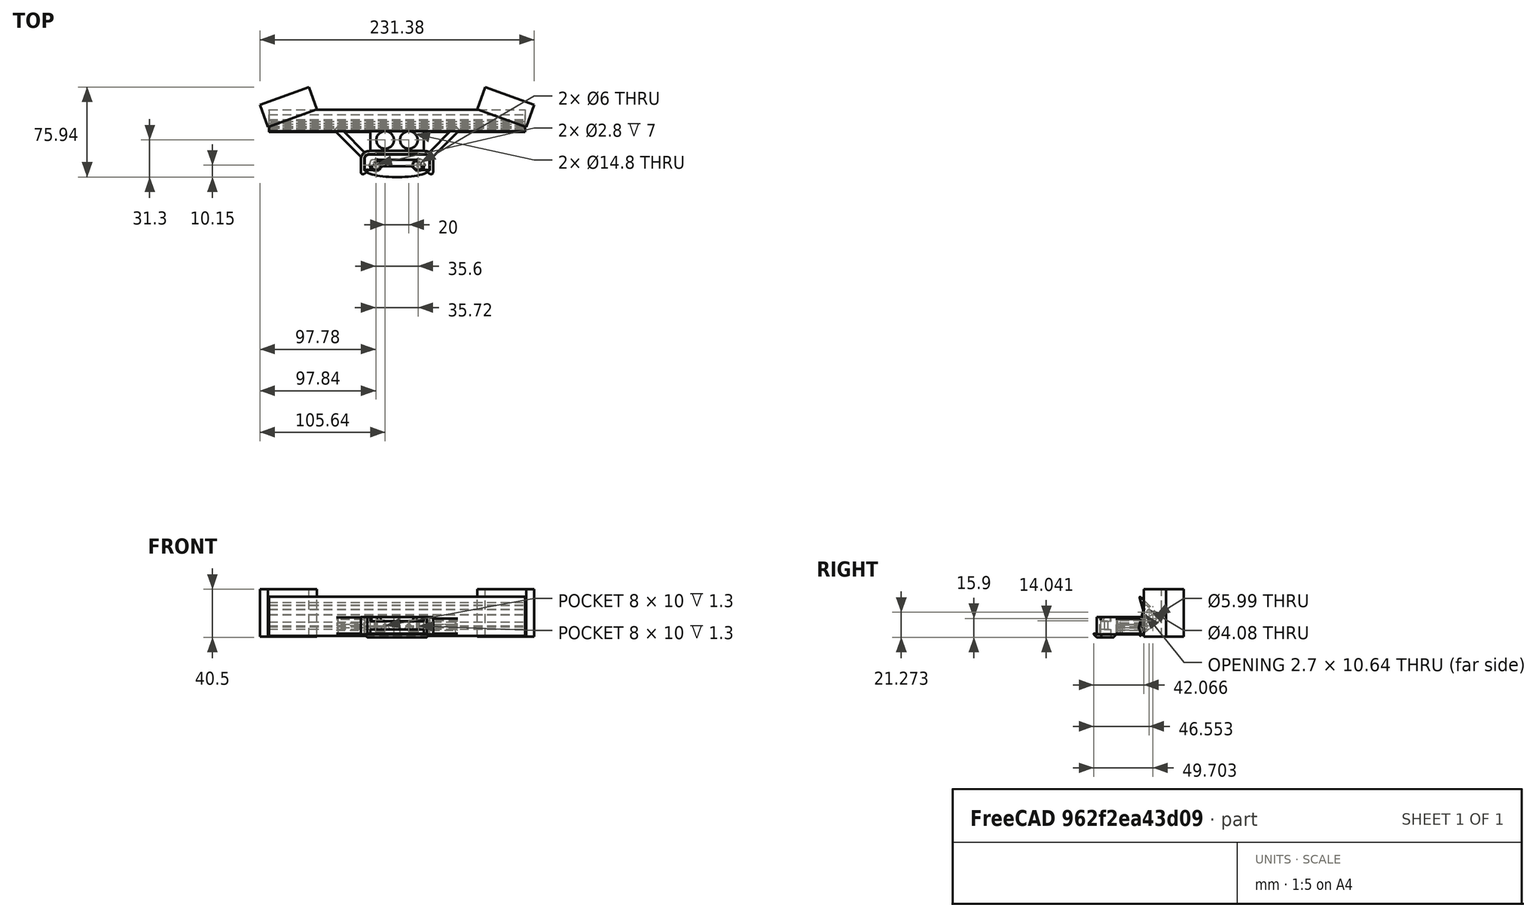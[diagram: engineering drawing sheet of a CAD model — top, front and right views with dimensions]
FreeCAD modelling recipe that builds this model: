
FCSTD DOCUMENT  (FreeCAD 0.21R0.20.1)
Label: 056
License: All rights reserved
LicenseURL: http://en.wikipedia.org/wiki/All_rights_reserved
objects: Part::Cylinder×20, Part::MultiFuse×13, Sketcher::SketchObject×7, Part::Extrusion×7, Part::Box×7, Part::Fillet×5, Part::Cut×4, Part::Chamfer×2
note: 65 computed .brp shape members not serialized (recipe doc carries the construction recipe); baked Part::Feature solids carry a one-line shape summary decoded from their .brp

FEATURE [Sketcher::SketchObject] Sketch  label="attatchmentPiece"
  FullyConstrained = true
  sketch-geometry (20):
    g0: LineSegment StartX=21.05 StartY=0 StartZ=0 EndX=21.05 EndY=-1 EndZ=0
    g1: LineSegment StartX=21.05 StartY=-1 StartZ=0 EndX=21.05 EndY=-4.3 EndZ=0
    g2: LineSegment StartX=-24.15 StartY=4.3 StartZ=0 EndX=21.05 EndY=4.3 EndZ=0
    g3: LineSegment StartX=21.05 StartY=0 StartZ=0 EndX=21.05 EndY=4.3 EndZ=0
    g4-g7: Circle x4 (B-spline internal-alignment scaffolding for g8; pole/knot coordinates omitted)
    g8: BSplineCurve PolesCount=4 KnotsCount=2 Degree=3 IsPeriodic=0
    g9: GeomPoint X=10.05 Y=-1 Z=0
    g10: GeomPoint X=14.55 Y=-4.3 Z=0
    g11: LineSegment StartX=10.05 StartY=-1 StartZ=0 EndX=-10.05 EndY=-1 EndZ=0
    g12: LineSegment StartX=14.55 StartY=-4.3 StartZ=0 EndX=21.05 EndY=-4.3 EndZ=0
    g13: LineSegment StartX=-24.15 StartY=4.3 StartZ=0 EndX=-24.15 EndY=-4.3 EndZ=0
    g14: LineSegment StartX=-13.15 StartY=-1 StartZ=0 EndX=-10.05 EndY=-1 EndZ=0
    g15: LineSegment StartX=-24.15 StartY=-4.3 StartZ=0 EndX=-19.35 EndY=-4.3 EndZ=0
    g16: LineSegment StartX=-19.35 StartY=-4.3 StartZ=0 EndX=-17.65 EndY=-4.3 EndZ=0
    g17: BSplineCurve PolesCount=4 KnotsCount=2 Degree=3 IsPeriodic=0
    g18: Circle CenterX=16.25 CenterY=0 CenterZ=0 NormalX=0 NormalY=0 NormalZ=1 AngleXU=0 Radius=1.4
    g19: Circle CenterX=-19.35 CenterY=0 CenterZ=0 NormalX=0 NormalY=0 NormalZ=1 AngleXU=0 Radius=1.4
  constraints (41):
    c: Vertical(g0)
    c: Coincident(g1,g0)
    c: Vertical(g1)
    c: Block(g0)
    c: Horizontal(g2)
    c: Vertical(g3)
    c: Coincident(g3,g2)
    c: Block(g2)
    c: Block(g3)
    c: Weight(g4) = 1
    c: Equal(g4,g5)
    c: Equal(g4,g6)
    c: Equal(g4,g7)
    c: InternalAlignment(g4-g7 -> g8) x4
    c: InternalAlignment(g9,g8)
    c: InternalAlignment(g10,g8)
    c: Block(g8)
    c: Coincident(g11,g8)
    c: Horizontal(g11)
    c: Coincident(g12,g8)
    c: Coincident(g12,g1)
    c: Horizontal(g12)
    c: Distance(g2) = 45.2
    c: Coincident(g13,g2)
    c: Vertical(g13)
    c: Horizontal(g14)
    c: Distance(g14) = 3.1
    c: Horizontal(g15)
    c: Block(g17)
    c: Coincident(g16,g15)
    c: Coincident(g16,g17)
    c: Horizontal(g16)
    c: Block(g16)
    c: Coincident(g17,g14)
    c: Block(g15)
    c: Block(g11)
    c: Block(g13)
    c: Distance(g15) = 4.8
    c: Distance(g16) = 1.7
    c: Block(g18)
    c: Block(g19)
FEATURE [Part::Extrusion] Extrude  label="attatchmentPiece001"
  Base = -> Sketch
  Dir = (0,0,1)
  DirMode = 2
  FaceMakerClass = Part::FaceMakerBullseye
  LengthFwd = 7
  LengthRev = 0
  Solid = true
  Symmetric = false
FEATURE [Sketcher::SketchObject] Sketch001  label="attatchmentPieceSurround"
  FullyConstrained = true
  sketch-geometry (18):
    g0: LineSegment StartX=25.85 StartY=-4.3 StartZ=0 EndX=21.05 EndY=-4.3 EndZ=0
    g1: LineSegment StartX=25.85 StartY=-4.3 StartZ=0 EndX=25.85 EndY=4.3 EndZ=0
    g2: LineSegment StartX=-21.05 StartY=8.9 StartZ=0 EndX=21.05 EndY=8.9 EndZ=0
    g3: Circle CenterX=21.05 CenterY=8.9 CenterZ=0 NormalX=0 NormalY=0 NormalZ=1 AngleXU=0 Radius=1
    g4: Circle CenterX=25.85 CenterY=8.9 CenterZ=0 NormalX=0 NormalY=0 NormalZ=1 AngleXU=0 Radius=1
    g5: Circle CenterX=25.85 CenterY=4.3 CenterZ=0 NormalX=0 NormalY=0 NormalZ=1 AngleXU=0 Radius=1
    g6: BSplineCurve PolesCount=3 KnotsCount=2 Degree=2 IsPeriodic=0
    g7: GeomPoint X=21.05 Y=8.9 Z=0
    g8: GeomPoint X=25.85 Y=4.3 Z=0
    g9: ArcOfCircle CenterX=19.45 CenterY=2.7 CenterZ=0 NormalX=0 NormalY=0 NormalZ=1 AngleXU=0 Radius=1.6 StartAngle=0 EndAngle=1.5708
    g10: LineSegment StartX=21.05 StartY=2.7 StartZ=0 EndX=21.05 EndY=-4.3 EndZ=0
    g11: BSplineCurve PolesCount=3 KnotsCount=2 Degree=2 IsPeriodic=0
    g12: LineSegment StartX=-28.95 StartY=-4.3 StartZ=0 EndX=-28.95 EndY=4.3 EndZ=0
    g13: LineSegment StartX=-24.15 StartY=-4.3 StartZ=0 EndX=-28.95 EndY=-4.3 EndZ=0
    g14: LineSegment StartX=-24.15 StartY=2.7 StartZ=0 EndX=-24.15 EndY=-4.3 EndZ=0
    g15: ArcOfCircle CenterX=-22.55 CenterY=2.7 CenterZ=0 NormalX=0 NormalY=0 NormalZ=1 AngleXU=0 Radius=1.6 StartAngle=1.5708 EndAngle=3.14159
    g16: LineSegment StartX=-24.15 StartY=8.9 StartZ=0 EndX=-21.05 EndY=8.9 EndZ=0
    g17: LineSegment StartX=-22.55 StartY=4.3 StartZ=0 EndX=19.45 EndY=4.3 EndZ=0
  constraints (38):
    c: Horizontal(g0)
    c: Vertical(g1)
    c: Coincident(g1,g0)
    c: Horizontal(g2)
    c: Distance(g2) = 42.1
    c: Block(g2)
    c: Coincident(g6,g2)
    c: Weight(g3) = 1
    c: Equal(g3,g4)
    c: Equal(g3,g5)
    c: Coincident(g6,g1)
    c: InternalAlignment(g3,g6)
    c: InternalAlignment(g4,g6)
    c: InternalAlignment(g5,g6)
    c: InternalAlignment(g7,g6)
    c: InternalAlignment(g8,g6)
    c: Block(g0)
    c: Block(g6)
    c: Block(g9)
    c: Coincident(g10,g9)
    c: Coincident(g10,g0)
    c: Vertical(g10)
    c: Horizontal(g13)
    c: Coincident(g12,g13)
    c: Vertical(g12)
    c: Coincident(g11,g12)
    c: Block(g12)
    c: Block(g11)
    c: Block(g15)
    c: Coincident(g14,g15)
    c: Coincident(g14,g13)
    c: Vertical(g14)
    c: Coincident(g16,g11)
    c: Coincident(g16,g2)
    c: Horizontal(g16)
    c: Coincident(g17,g15)
    c: Coincident(g17,g9)
    c: Horizontal(g17)
FEATURE [Part::Extrusion] Extrude001  label="attatchmentPieceSurround001"
  Base = -> Sketch001
  Dir = (0,0,1)
  DirMode = 2
  FaceMakerClass = Part::FaceMakerBullseye
  LengthFwd = 14.7
  LengthRev = 0
  Placement = pos=(0,0,-4.1) rot=(0,0,1;0rad)
  Solid = true
  Symmetric = false
FEATURE [Sketcher::SketchObject] Sketch002  label="attatchmentPieceEndScrewHoleCaps"
  FullyConstrained = true
  sketch-geometry (10):
    g0: ArcOfCircle CenterX=16.25 CenterY=0 CenterZ=0 NormalX=0 NormalY=0 NormalZ=1 AngleXU=0 Radius=4.3 StartAngle=2.05456 EndAngle=5.79942
    g1: LineSegment StartX=14.25 StartY=3.80657 StartZ=0 EndX=14.25 EndY=6 EndZ=0
    g2: LineSegment StartX=20.0566 StartY=-2 StartZ=0 EndX=22.25 EndY=-2 EndZ=0
    g3: LineSegment StartX=22.25 StartY=-2 StartZ=0 EndX=22.25 EndY=6 EndZ=0
    g4: LineSegment StartX=14.25 StartY=6 StartZ=0 EndX=22.25 EndY=6 EndZ=0
    g5: LineSegment StartX=-25.35 StartY=-2 StartZ=0 EndX=-25.35 EndY=6 EndZ=0
    g6: LineSegment StartX=-25.35 StartY=-2 StartZ=0 EndX=-23.1566 EndY=-2 EndZ=0
    g7: LineSegment StartX=-17.35 StartY=6 StartZ=0 EndX=-25.35 EndY=6 EndZ=0
    g8: LineSegment StartX=-17.35 StartY=3.80657 StartZ=0 EndX=-17.35 EndY=6 EndZ=0
    g9: ArcOfCircle CenterX=-19.35 CenterY=0 CenterZ=0 NormalX=0 NormalY=0 NormalZ=1 AngleXU=0 Radius=4.3 StartAngle=3.62536 EndAngle=7.37022
  constraints (25):
    c: Block(g0)
    c: Vertical(g1)
    c: Horizontal(g2)
    c: Coincident(g3,g2)
    c: Vertical(g3)
    c: Coincident(g4,g1)
    c: Horizontal(g4)
    c: Coincident(g3,g4)
    c: Block(g4)
    c: Block(g3)
    c: Coincident(g0,g1)
    c: Coincident(g0,g2)
    c: Block(g1)
    c: Block(g9)
    c: Horizontal(g6)
    c: Vertical(g8)
    c: Coincident(g7,g8)
    c: Horizontal(g7)
    c: Coincident(g5,g6)
    c: Vertical(g5)
    c: Coincident(g5,g7)
    c: Block(g7)
    c: Block(g5)
    c: Coincident(g9,g6)
    c: Coincident(g9,g8)
FEATURE [Part::Extrusion] Extrude002  label="attatchmentPieceEndScrewHoleCaps001"
  Base = -> Sketch002
  Dir = (0,0,1)
  DirMode = 2
  FaceMakerClass = Part::FaceMakerBullseye
  LengthFwd = 3.6
  LengthRev = 0
  Placement = pos=(0,0,7) rot=(0,0,1;0rad)
  Solid = true
  Symmetric = false
FEATURE [Sketcher::SketchObject] Sketch003  label="mainBumpperPieceAttatchment"
  FullyConstrained = true
  sketch-geometry (42):
    g0: Circle CenterX=28.85 CenterY=4.3 CenterZ=0 NormalX=0 NormalY=0 NormalZ=1 AngleXU=0 Radius=1
    g1: Circle CenterX=28.85 CenterY=11.9 CenterZ=0 NormalX=0 NormalY=0 NormalZ=1 AngleXU=0 Radius=1
    g2: Circle CenterX=21.05 CenterY=11.9 CenterZ=0 NormalX=0 NormalY=0 NormalZ=1 AngleXU=0 Radius=1
    g3: BSplineCurve PolesCount=3 KnotsCount=2 Degree=2 IsPeriodic=0
    g4: GeomPoint X=28.85 Y=4.3 Z=0
    g5: GeomPoint X=21.05 Y=11.9 Z=0
    g6: LineSegment StartX=-21.05 StartY=11.9 StartZ=0 EndX=21.05 EndY=11.9 EndZ=0
    g7: LineSegment StartX=28.85 StartY=4.3 StartZ=0 EndX=28.85 EndY=-4.3 EndZ=0
    g8: Circle CenterX=21.05 CenterY=9.2 CenterZ=0 NormalX=0 NormalY=0 NormalZ=1 AngleXU=0 Radius=1
    g9: Circle CenterX=26.15 CenterY=9.2 CenterZ=0 NormalX=0 NormalY=0 NormalZ=1 AngleXU=0 Radius=1
    g10: Circle CenterX=26.15 CenterY=4.3 CenterZ=0 NormalX=0 NormalY=0 NormalZ=1 AngleXU=0 Radius=1
    g11: BSplineCurve PolesCount=3 KnotsCount=2 Degree=2 IsPeriodic=0
    g12: GeomPoint X=21.05 Y=9.2 Z=0
    g13: GeomPoint X=26.15 Y=4.3 Z=0
    g14: LineSegment StartX=-21.05 StartY=9.2 StartZ=0 EndX=21.05 EndY=9.2 EndZ=0
    g15: LineSegment StartX=26.15 StartY=-4.3 StartZ=0 EndX=26.15 EndY=4.3 EndZ=0
    g16: LineSegment StartX=26.15 StartY=-4.3 StartZ=0 EndX=26.15 EndY=-4.6 EndZ=0
    g17: LineSegment StartX=23.45 StartY=-4.6 StartZ=0 EndX=26.15 EndY=-4.6 EndZ=0
    g18: LineSegment StartX=28.85 StartY=-4.3 StartZ=0 EndX=28.85 EndY=-7.9 EndZ=0
    g19: LineSegment StartX=23.45 StartY=-4.6 StartZ=0 EndX=23.45 EndY=-5.3 EndZ=0
    g20: Circle CenterX=28.85 CenterY=-7.9 CenterZ=0 NormalX=0 NormalY=0 NormalZ=1 AngleXU=0 Radius=1
    g21: Circle CenterX=26.15 CenterY=-8.2 CenterZ=0 NormalX=0 NormalY=0 NormalZ=1 AngleXU=0 Radius=1
    g22: Circle CenterX=23.45 CenterY=-5.3 CenterZ=0 NormalX=0 NormalY=0 NormalZ=1 AngleXU=0 Radius=1
    g23: BSplineCurve PolesCount=3 KnotsCount=2 Degree=2 IsPeriodic=0
    g24: GeomPoint X=28.85 Y=-7.9 Z=0
    g25: GeomPoint X=23.45 Y=-5.3 Z=0
    g26: LineSegment StartX=-21.05 StartY=9.2 StartZ=0 EndX=-24.15 EndY=9.2 EndZ=0
    g27: BSplineCurve PolesCount=3 KnotsCount=2 Degree=2 IsPeriodic=0
    g28: LineSegment StartX=-29.25 StartY=-4.3 StartZ=0 EndX=-29.25 EndY=-4.6 EndZ=0
    g29: LineSegment StartX=-29.25 StartY=-4.6 StartZ=0 EndX=-26.55 EndY=-4.6 EndZ=0
    g30: LineSegment StartX=-31.95 StartY=-4.3 StartZ=0 EndX=-31.95 EndY=-7.9 EndZ=0
    g31: LineSegment StartX=-26.55 StartY=-4.6 StartZ=0 EndX=-26.55 EndY=-5.3 EndZ=0
    g32: Circle CenterX=-31.95 CenterY=-7.9 CenterZ=0 NormalX=0 NormalY=0 NormalZ=1 AngleXU=0 Radius=1
    g33: Circle CenterX=-29.25 CenterY=-8.2 CenterZ=0 NormalX=0 NormalY=0 NormalZ=1 AngleXU=0 Radius=1
    g34: Circle CenterX=-26.55 CenterY=-5.3 CenterZ=0 NormalX=0 NormalY=0 NormalZ=1 AngleXU=0 Radius=1
    g35: BSplineCurve PolesCount=3 KnotsCount=2 Degree=2 IsPeriodic=0
    g36: GeomPoint X=-31.95 Y=-7.9 Z=0
    g37: GeomPoint X=-26.55 Y=-5.3 Z=0
    g38: LineSegment StartX=-31.95 StartY=4.3 StartZ=0 EndX=-31.95 EndY=-4.3 EndZ=0
    g39: LineSegment StartX=-29.25 StartY=-4.3 StartZ=0 EndX=-29.25 EndY=4.3 EndZ=0
    g40: BSplineCurve PolesCount=3 KnotsCount=2 Degree=2 IsPeriodic=0
    g41: LineSegment StartX=-21.05 StartY=11.9 StartZ=0 EndX=-24.15 EndY=11.9 EndZ=0
  constraints (78):
    c: Weight(g0) = 1
    c: Equal(g0,g1)
    c: Equal(g0,g2)
    c: InternalAlignment(g0,g3)
    c: InternalAlignment(g1,g3)
    c: InternalAlignment(g2,g3)
    c: InternalAlignment(g4,g3)
    c: InternalAlignment(g5,g3)
    c: Block(g3)
    c: Horizontal(g6)
    c: Vertical(g7)
    c: Block(g7)
    c: Block(g6)
    c: Weight(g8) = 1
    c: Equal(g8,g9)
    c: Equal(g8,g10)
    c: InternalAlignment(g8,g11)
    c: InternalAlignment(g9,g11)
    c: InternalAlignment(g10,g11)
    c: InternalAlignment(g12,g11)
    c: InternalAlignment(g13,g11)
    c: Horizontal(g14)
    c: Vertical(g15)
    c: Block(g11)
    c: Block(g15)
    c: Block(g14)
    c: Coincident(g16,g15)
    c: Vertical(g16)
    c: Distance(g16) = 0.3
    c: Horizontal(g17)
    c: Coincident(g17,g16)
    c: Coincident(g18,g7)
    c: Vertical(g18)
    c: Distance(g18) = 3.6
    c: Vertical(g19)
    c: Coincident(g19,g17)
    c: Coincident(g23,g18)
    c: Weight(g20) = 1
    c: Equal(g20,g21)
    c: Equal(g20,g22)
    c: Coincident(g23,g19)
    c: InternalAlignment(g20,g23)
    c: InternalAlignment(g21,g23)
    c: InternalAlignment(g22,g23)
    c: InternalAlignment(g24,g23)
    c: InternalAlignment(g25,g23)
    c: Block(g23)
    c: Horizontal(g26)
    c: Distance(g26) = 3.1
    c: Block(g27)
    c: Vertical(g38)
    c: Block(g38)
    c: Vertical(g39)
    c: Block(g40)
    c: Block(g39)
    c: Vertical(g28)
    c: Coincident(g28,g39)
    c: Coincident(g29,g28)
    c: Horizontal(g29)
    c: Vertical(g30)
    c: Coincident(g30,g38)
    c: Coincident(g31,g29)
    c: Vertical(g31)
    c: Coincident(g35,g30)
    c: Equal(g32,g33)
    c: Equal(g32,g34)
    c: Coincident(g35,g31)
    c: InternalAlignment(g32,g35)
    c: InternalAlignment(g33,g35)
    c: InternalAlignment(g34,g35)
    c: InternalAlignment(g36,g35)
    c: InternalAlignment(g37,g35)
    c: Block(g35)
    c: Coincident(g40,g26)
    c: Block(g29)
    c: Horizontal(g41)
    c: Equal(g26,g41) = 3.1
    c: Coincident(g41,g6)
FEATURE [Part::Box] Box  label="bumpperExtension"
  AttacherType = Attacher::AttachEngine3D
  Height = 14.7
  Length = 45.2
  Placement = pos=(-24.15,11.9,-4.1) rot=(0,0,1;0rad)
  Width = 18
FEATURE [Sketcher::SketchObject] Sketch004  label="bumpperMain"
  FullyConstrained = true
  Placement = pos=(0,0,0) rot=(0.57735,0.57735,0.57735;2.0944rad)
  sketch-geometry (62):
    g0: Circle CenterX=-3.12329 CenterY=2.49901 CenterZ=0 NormalX=0 NormalY=0 NormalZ=1 AngleXU=0 Radius=1
    g1: Circle CenterX=0 CenterY=0 CenterZ=0 NormalX=0 NormalY=0 NormalZ=1 AngleXU=0 Radius=1
    g2: Circle CenterX=-1.35243 CenterY=3.60648 CenterZ=0 NormalX=0 NormalY=0 NormalZ=1 AngleXU=0 Radius=1
    g3: BSplineCurve PolesCount=3 KnotsCount=2 Degree=2 IsPeriodic=0
    g4: GeomPoint X=-3.12329 Y=2.49901 Z=0
    g5: GeomPoint X=-1.35243 Y=3.60648 Z=0
    g6: Circle CenterX=-2.83953 CenterY=33.0261 CenterZ=0 NormalX=0 NormalY=0 NormalZ=1 AngleXU=0 Radius=1
    g7: Circle CenterX=0 CenterY=35.8434 CenterZ=0 NormalX=0 NormalY=0 NormalZ=1 AngleXU=0 Radius=1
    g8: Circle CenterX=-1.15771 CenterY=32.0146 CenterZ=0 NormalX=0 NormalY=0 NormalZ=1 AngleXU=0 Radius=1
    g9: BSplineCurve PolesCount=3 KnotsCount=2 Degree=2 IsPeriodic=0
    g10: GeomPoint X=-2.83953 Y=33.0261 Z=0
    g11: GeomPoint X=-1.15771 Y=32.0146 Z=0
    g12: Circle CenterX=-18.2963 CenterY=17.6904 CenterZ=0 NormalX=0 NormalY=0 NormalZ=1 AngleXU=0 Radius=1
    g13: Circle CenterX=-20 CenterY=16 CenterZ=0 NormalX=0 NormalY=0 NormalZ=1 AngleXU=0 Radius=1
    g14: Circle CenterX=-18.1259 CenterY=14.5008 CenterZ=0 NormalX=0 NormalY=0 NormalZ=1 AngleXU=0 Radius=1
    g15: BSplineCurve PolesCount=3 KnotsCount=2 Degree=2 IsPeriodic=0
    g16: GeomPoint X=-18.2963 Y=17.6904 Z=0
    g17: GeomPoint X=-18.1259 Y=14.5008 Z=0
    g18: LineSegment StartX=-18.2963 StartY=17.6904 StartZ=0 EndX=-2.83953 EndY=33.0261 EndZ=0
    g19: LineSegment StartX=-18.1259 StartY=14.5008 StartZ=0 EndX=-3.12329 EndY=2.49901 EndZ=0
    g20: Circle CenterX=-11.9527 CenterY=16 CenterZ=0 NormalX=0 NormalY=0 NormalZ=1 AngleXU=0 Radius=2.99582
    g21: Circle CenterX=-8.803 CenterY=21.3731 CenterZ=0 NormalX=0 NormalY=0 NormalZ=1 AngleXU=0 Radius=2.03939
    g22: Circle CenterX=-6.23123 CenterY=25.4475 CenterZ=0 NormalX=0 NormalY=0 NormalZ=1 AngleXU=0 Radius=1.69309
    g23: Circle CenterX=-4.38186 CenterY=28.6261 CenterZ=0 NormalX=0 NormalY=0 NormalZ=1 AngleXU=0 Radius=1.13029
    g24: Circle CenterX=-8.28033 CenterY=11.4296 CenterZ=0 NormalX=0 NormalY=0 NormalZ=1 AngleXU=0 Radius=1.57213
    g25: Circle CenterX=-5.93972 CenterY=8.22213 CenterZ=0 NormalX=0 NormalY=0 NormalZ=1 AngleXU=0 Radius=1.28743
    g26: Circle CenterX=-3.47023 CenterY=24.3665 CenterZ=0 NormalX=0 NormalY=0 NormalZ=1 AngleXU=0 Radius=1
    g27: Circle CenterX=-3.90437 CenterY=22.9307 CenterZ=0 NormalX=0 NormalY=0 NormalZ=1 AngleXU=0 Radius=1
    g28: Circle CenterX=-3.53772 CenterY=21.4762 CenterZ=0 NormalX=0 NormalY=0 NormalZ=1 AngleXU=0 Radius=1
    g29: BSplineCurve PolesCount=3 KnotsCount=2 Degree=2 IsPeriodic=0
    g30: GeomPoint X=-3.47023 Y=24.3665 Z=0
    g31: GeomPoint X=-3.53772 Y=21.4762 Z=0
    g32: LineSegment StartX=-1.15771 StartY=32.0146 StartZ=0 EndX=-3.47023 EndY=24.3665 EndZ=0
    g33: Circle CenterX=-5.41867 CenterY=17.9226 CenterZ=0 NormalX=0 NormalY=0 NormalZ=1 AngleXU=0 Radius=1
    g34: Circle CenterX=-6 CenterY=16 CenterZ=0 NormalX=0 NormalY=0 NormalZ=1 AngleXU=0 Radius=1
    g35: Circle CenterX=-5.22753 CenterY=13.9401 CenterZ=0 NormalX=0 NormalY=0 NormalZ=1 AngleXU=0 Radius=1
    g36: BSplineCurve PolesCount=3 KnotsCount=2 Degree=2 IsPeriodic=0
    g37: GeomPoint X=-5.41867 Y=17.9226 Z=0
    g38: GeomPoint X=-5.22753 Y=13.9401 Z=0
    g39: Circle CenterX=-3.98946 CenterY=10.6386 CenterZ=0 NormalX=0 NormalY=0 NormalZ=1 AngleXU=0 Radius=1
    g40: Circle CenterX=-2.58497 CenterY=6.89324 CenterZ=0 NormalX=0 NormalY=0 NormalZ=1 AngleXU=0 Radius=1
    g41: Circle CenterX=-3.11001 CenterY=10.8586 CenterZ=0 NormalX=0 NormalY=0 NormalZ=1 AngleXU=0 Radius=1
    g42: BSplineCurve PolesCount=3 KnotsCount=2 Degree=2 IsPeriodic=0
    g43: GeomPoint X=-3.98946 Y=10.6386 Z=0
    g44: GeomPoint X=-3.11001 Y=10.8586 Z=0
    g45: Circle CenterX=-1.35243 CenterY=3.60648 CenterZ=0 NormalX=0 NormalY=0 NormalZ=1 AngleXU=0 Radius=1
    g46: Circle CenterX=-1.76142 CenterY=4.69712 CenterZ=0 NormalX=0 NormalY=0 NormalZ=1 AngleXU=0 Radius=1
    g47: Circle CenterX=-1.05937 CenterY=5.79125 CenterZ=0 NormalX=0 NormalY=0 NormalZ=1 AngleXU=0 Radius=1
    g48: BSplineCurve PolesCount=3 KnotsCount=2 Degree=2 IsPeriodic=0
    g49: GeomPoint X=-1.35243 Y=3.60648 Z=0
    g50: GeomPoint X=-1.05937 Y=5.79125 Z=0
    g51: Circle CenterX=-0.519336 CenterY=6.6329 CenterZ=0 NormalX=0 NormalY=0 NormalZ=1 AngleXU=0 Radius=1
    g52: Circle CenterX=0 CenterY=7.44228 CenterZ=0 NormalX=0 NormalY=0 NormalZ=1 AngleXU=0 Radius=1
    g53: Circle CenterX=-0.244436 CenterY=8.41194 CenterZ=0 NormalX=0 NormalY=0 NormalZ=1 AngleXU=0 Radius=1
    g54: BSplineCurve PolesCount=3 KnotsCount=2 Degree=2 IsPeriodic=0
    g55: GeomPoint X=-0.519336 Y=6.6329 Z=0
    g56: GeomPoint X=-0.244436 Y=8.41194 Z=0
    g57: LineSegment StartX=-3.53772 StartY=21.4762 StartZ=0 EndX=-0.244436 EndY=8.41194 EndZ=0
    g58: LineSegment StartX=-5.22753 StartY=13.9401 StartZ=0 EndX=-3.98946 EndY=10.6386 EndZ=0
    g59: LineSegment StartX=-1.05937 StartY=5.79125 StartZ=0 EndX=-0.519336 EndY=6.6329 EndZ=0
    g60: BSplineCurve PolesCount=3 KnotsCount=2 Degree=2 IsPeriodic=0
    g61: LineSegment StartX=-4.0304 StartY=17.8099 StartZ=0 EndX=-3.11001 EndY=10.8586 EndZ=0
  constraints (96):
    c: Weight(g0) = 1
    c: Equal(g0,g1)
    c: Equal(g0,g2)
    c: InternalAlignment(g0,g3)
    c: InternalAlignment(g1,g3)
    c: InternalAlignment(g2,g3)
    c: InternalAlignment(g4,g3)
    c: InternalAlignment(g5,g3)
    c: Block(g3)
    c: Weight(g6) = 1
    c: Equal(g6,g7)
    c: Equal(g6,g8)
    c: InternalAlignment(g6,g9)
    c: InternalAlignment(g7,g9)
    c: InternalAlignment(g8,g9)
    c: InternalAlignment(g10,g9)
    c: InternalAlignment(g11,g9)
    c: Block(g9)
    c: Weight(g12) = 1
    c: Equal(g12,g13)
    c: Equal(g12,g14)
    c: InternalAlignment(g12,g15)
    c: InternalAlignment(g13,g15)
    c: InternalAlignment(g14,g15)
    c: InternalAlignment(g16,g15)
    c: InternalAlignment(g17,g15)
    c: Block(g15)
    c: Coincident(g18,g15)
    c: Coincident(g18,g9)
    c: Coincident(g19,g15)
    c: Coincident(g19,g3)
    c: Block(g25)
    c: Block(g24)
    c: Block(g20)
    c: Block(g21)
    c: Block(g22)
    c: Block(g23)
    c: Weight(g26) = 1
    c: Equal(g26,g27)
    c: Equal(g26,g28)
    c: InternalAlignment(g26,g29)
    c: InternalAlignment(g27,g29)
    c: InternalAlignment(g28,g29)
    c: InternalAlignment(g30,g29)
    c: InternalAlignment(g31,g29)
    c: Block(g29)
    c: Coincident(g32,g9)
    c: Coincident(g32,g29)
    c: Weight(g33) = 1
    c: Equal(g33,g34)
    c: Equal(g33,g35)
    c: InternalAlignment(g33,g36)
    c: InternalAlignment(g34,g36)
    c: InternalAlignment(g35,g36)
    c: InternalAlignment(g37,g36)
    c: InternalAlignment(g38,g36)
    c: Block(g36)
    c: Weight(g39) = 1
    c: Equal(g39,g40)
    c: Equal(g39,g41)
    c: InternalAlignment(g39,g42)
    c: InternalAlignment(g40,g42)
    c: InternalAlignment(g41,g42)
    c: InternalAlignment(g43,g42)
    c: InternalAlignment(g44,g42)
    c: Block(g42)
    c: Coincident(g48,g3)
    c: Weight(g45) = 1
    c: Equal(g45,g46)
    c: Equal(g45,g47)
    c: InternalAlignment(g45,g48)
    c: InternalAlignment(g46,g48)
    c: InternalAlignment(g47,g48)
    c: InternalAlignment(g49,g48)
    c: InternalAlignment(g50,g48)
    c: Block(g48)
    c: Weight(g51) = 1
    c: Equal(g51,g52)
    c: Equal(g51,g53)
    c: InternalAlignment(g51,g54)
    c: InternalAlignment(g52,g54)
    c: InternalAlignment(g53,g54)
    c: InternalAlignment(g55,g54)
    c: InternalAlignment(g56,g54)
    c: Block(g54)
    c: Coincident(g57,g29)
    c: Coincident(g57,g54)
    c: Block(g57)
    c: Coincident(g58,g36)
    c: Coincident(g58,g42)
    c: Coincident(g59,g48)
    c: Coincident(g59,g54)
    c: Block(g60)
    c: Coincident(g60,g36)
    c: Coincident(g61,g60)
    c: Coincident(g61,g42)
FEATURE [Part::Extrusion] Extrude004  label="bumpperMain001"
  Base = -> Sketch004
  Dir = (1,0,0)
  DirMode = 2
  FaceMakerClass = Part::FaceMakerBullseye
  LengthFwd = 216
  LengthRev = 0
  Placement = pos=(106.45,27.6,-6.6) rot=(0,0,1;3.14159rad)
  Solid = true
  Symmetric = false
FEATURE [Sketcher::SketchObject] Sketch005  label="attatchmentPieceBottom"
  FullyConstrained = true
  sketch-geometry (20):
    g0: LineSegment StartX=25.85 StartY=-4.3 StartZ=0 EndX=25.85 EndY=4.3 EndZ=0
    g1: LineSegment StartX=-21.05 StartY=8.9 StartZ=0 EndX=21.05 EndY=8.9 EndZ=0
    g2: Circle CenterX=21.05 CenterY=8.9 CenterZ=0 NormalX=0 NormalY=0 NormalZ=1 AngleXU=0 Radius=1
    g3: Circle CenterX=25.85 CenterY=8.9 CenterZ=0 NormalX=0 NormalY=0 NormalZ=1 AngleXU=0 Radius=1
    g4: Circle CenterX=25.85 CenterY=4.3 CenterZ=0 NormalX=0 NormalY=0 NormalZ=1 AngleXU=0 Radius=1
    g5: BSplineCurve PolesCount=3 KnotsCount=2 Degree=2 IsPeriodic=0
    g6: GeomPoint X=21.05 Y=8.9 Z=0
    g7: GeomPoint X=25.85 Y=4.3 Z=0
    g8: BSplineCurve PolesCount=3 KnotsCount=2 Degree=2 IsPeriodic=0
    g9: LineSegment StartX=-28.95 StartY=-4.3 StartZ=0 EndX=-28.95 EndY=4.3 EndZ=0
    g10: LineSegment StartX=-24.15 StartY=8.9 StartZ=0 EndX=-21.05 EndY=8.9 EndZ=0
    g11: Circle CenterX=-19.41 CenterY=0 CenterZ=0 NormalX=0 NormalY=0 NormalZ=1 AngleXU=0 Radius=3
    g12: Circle CenterX=16.3103 CenterY=0 CenterZ=0 NormalX=0 NormalY=0 NormalZ=1 AngleXU=0 Radius=3
    g13-g16: Circle x4 (B-spline internal-alignment scaffolding for g17; pole/knot coordinates omitted)
    g17: BSplineCurve PolesCount=4 KnotsCount=2 Degree=3 IsPeriodic=0
    g18: GeomPoint X=-28.95 Y=-4.3 Z=0
    g19: GeomPoint X=25.85 Y=-4.3 Z=0
  constraints (36):
    c: Vertical(g0)
    c: Horizontal(g1)
    c: Distance(g1) = 42.1
    c: Block(g1)
    c: Coincident(g5,g1)
    c: Weight(g2) = 1
    c: Equal(g2,g3)
    c: Equal(g2,g4)
    c: Coincident(g5,g0)
    c: InternalAlignment(g2,g5)
    c: InternalAlignment(g3,g5)
    c: InternalAlignment(g4,g5)
    c: InternalAlignment(g6,g5)
    c: InternalAlignment(g7,g5)
    c: Block(g5)
    c: Vertical(g9)
    c: Coincident(g8,g9)
    c: Block(g9)
    c: Block(g8)
    c: Coincident(g10,g8)
    c: Coincident(g10,g1)
    c: Horizontal(g10)
    c: PointOnObject(g12,g-1)
    c: PointOnObject(g11,g-1)
    c: Block(g11)
    c: Block(g12)
    c: Coincident(g17,g9)
    c: Weight(g13) = 1
    c: Equal(g13,g14)
    c: Equal(g13,g15)
    c: Equal(g13,g16)
    c: Coincident(g17,g0)
    c: InternalAlignment(g13-g16 -> g17) x4
    c: InternalAlignment(g18,g17)
    c: InternalAlignment(g19,g17)
    c: Block(g17)
FEATURE [Part::Extrusion] Extrude005  label="removeFromMainBumpperPieceAttatchment"
  Base = -> Sketch005
  Dir = (0,0,1)
  DirMode = 2
  FaceMakerClass = Part::FaceMakerBullseye
  LengthFwd = 3.2
  LengthRev = 0
  Placement = pos=(0,0,-6.2) rot=(0,0,1;0rad)
  Solid = true
  Symmetric = false
FEATURE [Part::Extrusion] Extrude006  label="mainBumpperPieceAttatchment001"
  Base = -> Sketch003
  Dir = (0,0,1)
  DirMode = 2
  FaceMakerClass = Part::FaceMakerBullseye
  LengthFwd = 14.7
  LengthRev = 0
  Placement = pos=(0,0,-4.1) rot=(0,0,1;0rad)
  Solid = true
  Symmetric = false
FEATURE [Part::Cylinder] Cylinder  label="removeFromBumpperExtension"
  Angle = 360
  AttacherType = Attacher::AttachEngine3D
  FirstAngle = 0
  Height = 20
  Placement = pos=(8.45,21.15,-8) rot=(0,0,1;0rad)
  Radius = 7.4
  SecondAngle = 0
FEATURE [Part::Cylinder] Cylinder001  label="removeFromBumpperExtension001"
  Angle = 360
  AttacherType = Attacher::AttachEngine3D
  FirstAngle = 0
  Height = 20
  Placement = pos=(-11.55,21.15,-8) rot=(0,0,1;0rad)
  Radius = 7.4
  SecondAngle = 0
FEATURE [Part::MultiFuse] Fusion  label="removeFromBumpperExtension002"
  Shapes = -> [Cylinder,Cylinder001]
FEATURE [Part::Cylinder] Cylinder002  label="removeFromBumpperExtension004"
  Angle = 360
  AttacherType = Attacher::AttachEngine3D
  FirstAngle = 0
  Height = 20
  Placement = pos=(8.45,21.15,-8) rot=(0,0,1;0rad)
  Radius = 7.4
  SecondAngle = 0
FEATURE [Part::Cylinder] Cylinder003  label="removeFromBumpperExtension005"
  Angle = 360
  AttacherType = Attacher::AttachEngine3D
  FirstAngle = 0
  Height = 20
  Placement = pos=(-11.55,21.15,-8) rot=(0,0,1;0rad)
  Radius = 7.4
  SecondAngle = 0
FEATURE [Part::MultiFuse] Fusion001  label="removeFromBumpperMain"
  Shapes = -> [Cylinder002,Cylinder003]
FEATURE [Part::Cut] Cut  label="bumpperExtension001"
  Base = -> Box
  Tool = -> Fusion
FEATURE [Part::Fillet] Fillet  label="bumpperExtension002"
  Base = -> Cut
  Edges = 4 edges r=3: [Edge2,Edge4,Edge9,Edge14]
FEATURE [Part::Box] Box001  label="bumpperExtensionBumpHole"
  AttacherType = Attacher::AttachEngine3D
  Height = 10
  Length = 8
  Placement = pos=(8.45,9.2,-1.8) rot=(0,0,1;0rad)
  Width = 1.3
FEATURE [Part::Box] Box002  label="bumpperExtensionBumpHole001"
  AttacherType = Attacher::AttachEngine3D
  Height = 10
  Length = 8
  Placement = pos=(-19.55,9.2,-1.8) rot=(0,0,1;0rad)
  Width = 1.3
FEATURE [Part::Box] Box003  label="attatchmentPieceSurroundBump"
  AttacherType = Attacher::AttachEngine3D
  Height = 9.2
  Length = 7.2
  Placement = pos=(8.85,8.9,-1.4) rot=(0,0,1;0rad)
  Width = 1.3
FEATURE [Part::Box] Box004  label="attatchmentPieceSurroundBump001"
  AttacherType = Attacher::AttachEngine3D
  Height = 9.2
  Length = 7.2
  Placement = pos=(-19.15,8.9,-1.4) rot=(0,0,1;0rad)
  Width = 1.3
FEATURE [Part::MultiFuse] Fusion002  label="attatchmentPieceSurroundBump002"
  Placement = pos=(0,-0.4,0) rot=(0,0,1;0rad)
  Shapes = -> [Box004,Box003]
FEATURE [Part::MultiFuse] Fusion003  label="bumpperExtensionBumpHole002"
  Shapes = -> [Box002,Box001]
FEATURE [Part::Cut] Cut002  label="mainBumpperPieceAttatchment002"
  Base = -> Extrude006
  Tool = -> Fusion003
FEATURE [Part::Fillet] Fillet003  label="attatchmentPieceEndScrewHoleCaps002"
  Base = -> Extrude002
  Edges = 6 edges r=2.4: [Edge4,Edge7,Edge15,Edge25,Edge28,Edge30]
FEATURE [Part::Fillet] Fillet004  label="attatchmentPieceSurround002"
  Base = -> Extrude001
  Edges = 3 edges r=1.2: [Edge19,Edge25,Edge31]
FEATURE [Part::Fillet] Fillet006  label="mainBumpperPieceAttatchment003"
  Base = -> Cut002
  Edges = 2 edges r=1.6: [Edge2,Edge55]
FEATURE [Sketcher::SketchObject] Sketch006  label="attatchmentPieceBottom002"
  FullyConstrained = true
  sketch-geometry (20):
    g0: LineSegment StartX=25.85 StartY=-4.3 StartZ=0 EndX=25.85 EndY=4.3 EndZ=0
    g1: LineSegment StartX=-21.05 StartY=8.9 StartZ=0 EndX=21.05 EndY=8.9 EndZ=0
    g2: Circle CenterX=21.05 CenterY=8.9 CenterZ=0 NormalX=0 NormalY=0 NormalZ=1 AngleXU=0 Radius=1
    g3: Circle CenterX=25.85 CenterY=8.9 CenterZ=0 NormalX=0 NormalY=0 NormalZ=1 AngleXU=0 Radius=1
    g4: Circle CenterX=25.85 CenterY=4.3 CenterZ=0 NormalX=0 NormalY=0 NormalZ=1 AngleXU=0 Radius=1
    g5: BSplineCurve PolesCount=3 KnotsCount=2 Degree=2 IsPeriodic=0
    g6: GeomPoint X=21.05 Y=8.9 Z=0
    g7: GeomPoint X=25.85 Y=4.3 Z=0
    g8: BSplineCurve PolesCount=3 KnotsCount=2 Degree=2 IsPeriodic=0
    g9: LineSegment StartX=-28.95 StartY=-4.3 StartZ=0 EndX=-28.95 EndY=4.3 EndZ=0
    g10: LineSegment StartX=-24.15 StartY=8.9 StartZ=0 EndX=-21.05 EndY=8.9 EndZ=0
    g11: Circle CenterX=-19.41 CenterY=0 CenterZ=0 NormalX=0 NormalY=0 NormalZ=1 AngleXU=0 Radius=3
    g12: Circle CenterX=16.3103 CenterY=0 CenterZ=0 NormalX=0 NormalY=0 NormalZ=1 AngleXU=0 Radius=3
    g13-g16: Circle x4 (B-spline internal-alignment scaffolding for g17; pole/knot coordinates omitted)
    g17: BSplineCurve PolesCount=4 KnotsCount=2 Degree=3 IsPeriodic=0
    g18: GeomPoint X=-28.95 Y=-4.3 Z=0
    g19: GeomPoint X=25.85 Y=-4.3 Z=0
  constraints (36):
    c: Vertical(g0)
    c: Horizontal(g1)
    c: Distance(g1) = 42.1
    c: Block(g1)
    c: Coincident(g5,g1)
    c: Weight(g2) = 1
    c: Equal(g2,g3)
    c: Equal(g2,g4)
    c: Coincident(g5,g0)
    c: InternalAlignment(g2,g5)
    c: InternalAlignment(g3,g5)
    c: InternalAlignment(g4,g5)
    c: InternalAlignment(g6,g5)
    c: InternalAlignment(g7,g5)
    c: Block(g5)
    c: Vertical(g9)
    c: Coincident(g8,g9)
    c: Block(g9)
    c: Block(g8)
    c: Coincident(g10,g8)
    c: Coincident(g10,g1)
    c: Horizontal(g10)
    c: PointOnObject(g12,g-1)
    c: PointOnObject(g11,g-1)
    c: Block(g11)
    c: Block(g12)
    c: Coincident(g17,g9)
    c: Weight(g13) = 1
    c: Equal(g13,g14)
    c: Equal(g13,g15)
    c: Equal(g13,g16)
    c: Coincident(g17,g0)
    c: InternalAlignment(g13-g16 -> g17) x4
    c: InternalAlignment(g18,g17)
    c: InternalAlignment(g19,g17)
    c: Block(g17)
FEATURE [Part::Extrusion] Extrude007  label="attatchmentPieceBottom003"
  Base = -> Sketch006
  Dir = (0,0,1)
  DirMode = 2
  FaceMakerClass = Part::FaceMakerBullseye
  LengthFwd = 3.2
  LengthRev = 0
  Placement = pos=(0,0,-6.5) rot=(0,0,1;0rad)
  Solid = true
  Symmetric = false
FEATURE [Part::Cut] Cut003  label="mainBumpperPieceAttatchment004"
  Base = -> Fillet006
  Tool = -> Extrude005
FEATURE [Part::Chamfer] Chamfer
  Base = -> Extrude007
  Edges = 2 edges r=2.4: [Edge23,Edge26]
FEATURE [Part::Chamfer] Chamfer001  label="attatchmentPieceBottom004"
  Base = -> Chamfer
  Edges = 7 edges r=2.4: [Edge14,Edge15,Edge16,Edge17,Edge18,Edge19,Edge20]
FEATURE [Part::Fillet] Fillet007  label="attatchmentPieceBottom005"
  Base = -> Chamfer001
  Edges = 7 edges r=1.2: [Edge1,Edge2,Edge3,Edge4,Edge5,Edge6,Edge7]
FEATURE [Part::MultiFuse] Fusion007  label="attatchment"
  Shapes = -> [Fillet007,Fillet004,Fillet003,Fusion002,Extrude]
FEATURE [Part::Cylinder] Cylinder004  label="brace"
  Angle = 360
  AttacherType = Attacher::AttachEngine3D
  FirstAngle = 0
  Height = 32
  Placement = pos=(-42,0,0) rot=(0,1,0;1.5708rad)
  Radius = 2.4
  SecondAngle = 0
FEATURE [Part::Cylinder] Cylinder005  label="brace001"
  Angle = 360
  AttacherType = Attacher::AttachEngine3D
  FirstAngle = 0
  Height = 10
  Placement = pos=(29,0,0) rot=(0,1,0;1.5708rad)
  Radius = 2
  SecondAngle = 0
FEATURE [Part::Cylinder] Cylinder006  label="brace002"
  Angle = 360
  AttacherType = Attacher::AttachEngine3D
  FirstAngle = 0
  Height = 10
  Placement = pos=(-42,0,0) rot=(0,1,0;1.5708rad)
  Radius = 2
  SecondAngle = 0
FEATURE [Part::MultiFuse] Fusion008  label="leftBrace"
  Placement = pos=(-23,1.4,8) rot=(0,0,1;-0.785398rad)
  Shapes = -> [Cylinder004,Cylinder006]
FEATURE [Part::Cylinder] Cylinder007  label="brace003"
  Angle = 360
  AttacherType = Attacher::AttachEngine3D
  FirstAngle = 0
  Height = 32
  Placement = pos=(29,0,0) rot=(0,1,0;1.5708rad)
  Radius = 2.4
  SecondAngle = 0
FEATURE [Part::MultiFuse] Fusion009  label="rightBrace"
  Placement = pos=(6.4,-12,7) rot=(0,0,1;0.785398rad)
  Shapes = -> [Cylinder007,Cylinder005]
FEATURE [Part::Box] Box005  label="removeFromMainRight"
  AttacherType = Attacher::AttachEngine3D
  Height = 40
  Length = 44
  Placement = pos=(66,47,-6) rot=(0,0,1;-0.349066rad)
  Width = 20
FEATURE [Part::Box] Box006  label="removeFromMainLeft"
  AttacherType = Attacher::AttachEngine3D
  Height = 40
  Length = 44
  Placement = pos=(-110.35,31.95,-6) rot=(0,0,1;0.349066rad)
  Width = 20
FEATURE [Part::Cylinder] Cylinder008  label="brace004"
  Angle = 360
  AttacherType = Attacher::AttachEngine3D
  FirstAngle = 0
  Height = 32
  Placement = pos=(-42,0,0) rot=(0,1,0;1.5708rad)
  Radius = 2.4
  SecondAngle = 0
FEATURE [Part::Cylinder] Cylinder009  label="brace005"
  Angle = 360
  AttacherType = Attacher::AttachEngine3D
  FirstAngle = 0
  Height = 10
  Placement = pos=(-42,0,0) rot=(0,1,0;1.5708rad)
  Radius = 2
  SecondAngle = 0
FEATURE [Part::MultiFuse] Fusion010  label="leftBrace001"
  Placement = pos=(-23,1.4,-1) rot=(0,0,-1;0.785398rad)
  Shapes = -> [Cylinder008,Cylinder009]
FEATURE [Part::Cylinder] Cylinder010  label="brace006"
  Angle = 360
  AttacherType = Attacher::AttachEngine3D
  FirstAngle = 0
  Height = 10
  Placement = pos=(29,0,0) rot=(0,1,0;1.5708rad)
  Radius = 2
  SecondAngle = 0
FEATURE [Part::Cylinder] Cylinder011  label="brace007"
  Angle = 360
  AttacherType = Attacher::AttachEngine3D
  FirstAngle = 0
  Height = 32
  Placement = pos=(29,0,0) rot=(0,1,0;1.5708rad)
  Radius = 2.4
  SecondAngle = 0
FEATURE [Part::MultiFuse] Fusion011  label="rightBrace001"
  Placement = pos=(6.4,-12,-1) rot=(0,0,1;0.785398rad)
  Shapes = -> [Cylinder011,Cylinder010]
FEATURE [Part::Cylinder] Cylinder012  label="brace008"
  Angle = 360
  AttacherType = Attacher::AttachEngine3D
  FirstAngle = 0
  Height = 32
  Placement = pos=(-42,0,0) rot=(0,1,0;1.5708rad)
  Radius = 2.4
  SecondAngle = 0
FEATURE [Part::Cylinder] Cylinder013  label="brace009"
  Angle = 360
  AttacherType = Attacher::AttachEngine3D
  FirstAngle = 0
  Height = 10
  Placement = pos=(-42,0,0) rot=(0,1,0;1.5708rad)
  Radius = 2
  SecondAngle = 0
FEATURE [Part::MultiFuse] Fusion012  label="leftBrace002"
  Placement = pos=(-23,1.4,6) rot=(0,0,-1;0.785398rad)
  Shapes = -> [Cylinder012,Cylinder013]
FEATURE [Part::Cylinder] Cylinder014  label="brace010"
  Angle = 360
  AttacherType = Attacher::AttachEngine3D
  FirstAngle = 0
  Height = 10
  Placement = pos=(29,0,0) rot=(0,1,0;1.5708rad)
  Radius = 2
  SecondAngle = 0
FEATURE [Part::Cylinder] Cylinder015  label="brace011"
  Angle = 360
  AttacherType = Attacher::AttachEngine3D
  FirstAngle = 0
  Height = 32
  Placement = pos=(29,0,0) rot=(0,1,0;1.5708rad)
  Radius = 2.4
  SecondAngle = 0
FEATURE [Part::MultiFuse] Fusion013  label="rightBrace002"
  Placement = pos=(6.4,-12,5) rot=(0,0,1;0.785398rad)
  Shapes = -> [Cylinder015,Cylinder014]
FEATURE [Part::Cylinder] Cylinder016  label="brace012"
  Angle = 360
  AttacherType = Attacher::AttachEngine3D
  FirstAngle = 0
  Height = 10
  Placement = pos=(29,0,0) rot=(0,1,0;1.5708rad)
  Radius = 2
  SecondAngle = 0
FEATURE [Part::Cylinder] Cylinder017  label="brace013"
  Angle = 360
  AttacherType = Attacher::AttachEngine3D
  FirstAngle = 0
  Height = 32
  Placement = pos=(29,0,0) rot=(0,1,0;1.5708rad)
  Radius = 2.4
  SecondAngle = 0
FEATURE [Part::MultiFuse] Fusion014  label="rightBrace003"
  Placement = pos=(6.4,-12,2) rot=(0,0,1;0.785398rad)
  Shapes = -> [Cylinder017,Cylinder016]
FEATURE [Part::Cylinder] Cylinder018  label="brace014"
  Angle = 360
  AttacherType = Attacher::AttachEngine3D
  FirstAngle = 0
  Height = 32
  Placement = pos=(-42,0,0) rot=(0,1,0;1.5708rad)
  Radius = 2.4
  SecondAngle = 0
FEATURE [Part::Cylinder] Cylinder019  label="brace015"
  Angle = 360
  AttacherType = Attacher::AttachEngine3D
  FirstAngle = 0
  Height = 10
  Placement = pos=(-42,0,0) rot=(0,1,0;1.5708rad)
  Radius = 2
  SecondAngle = 0
FEATURE [Part::MultiFuse] Fusion015  label="leftBrace003"
  Placement = pos=(-23,1.4,2) rot=(0,0,-1;0.785398rad)
  Shapes = -> [Cylinder018,Cylinder019]
FEATURE [Part::Cut] Cut004
  Base = -> Extrude004
  Tool = -> Fusion001
